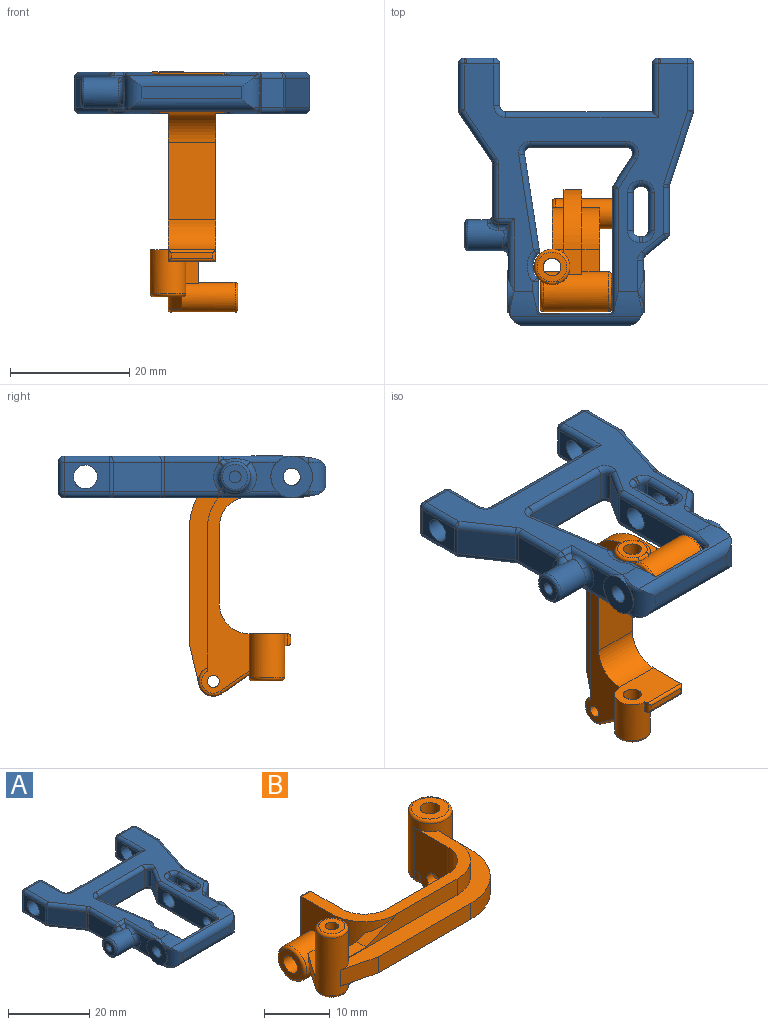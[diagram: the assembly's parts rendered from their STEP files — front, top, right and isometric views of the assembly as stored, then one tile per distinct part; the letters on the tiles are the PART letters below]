
ASSEMBLY  parts=2 mates=1
PART A: 193 faces, bbox 39.6x45x7 mm
  f0: cylinder r=1mm len=2.75mm, axis (0,1,0), area 1.5mm2, adj f15,f20,f177,f183
  f1: cylinder r=1mm len=2.75mm, axis (0,1,0), area 1.5mm2, adj f16,f26,f175,f186
  f2: cylinder r=1mm len=2.75mm, axis (0,-1,0), area 1.5mm2, adj f18,f23,f175,f183
  f3: plane 38.25x37.6mm, normal (0,0,1), area 421.9mm2, adj f7,f11,f21,f27,f57,f62,f65,f66
  f4: plane 38.25x37.6mm, normal (0,0,-1), area 421.9mm2, adj f8,f12,f24,f59,f63,f68,f69,f78
  f5: plane 16.75x2.05mm, normal (0,-1,0), area 34.3mm2, adj f14,f17,f184,f185
  f6: cylinder r=1mm len=2.75mm, axis (0,-1,0), area 1.5mm2, adj f13,f19,f177,f186
  f7: cylinder r=1mm len=20.85mm, axis (0,1,0), area 31.1mm2, adj f3,f54,f128,f186,f189
  f8: cylinder r=1mm len=20.85mm, axis (0,-1,0), area 31.1mm2, adj f4,f54,f131,f183,f187
  f9: cylinder r=1mm len=11.92mm, axis (1,0,0), area 7mm2, adj f36,f186,f189,f192
  f10: cylinder r=1mm len=11.92mm, axis (-1,0,0), area 7mm2, adj f36,f183,f187,f190
  f11: cylinder r=1mm len=5.15mm, axis (0,-1,0), area 6.4mm2, adj f3,f37,f139,f186,f192
  f12: cylinder r=1mm len=5.15mm, axis (0,1,0), area 6.4mm2, adj f4,f37,f140,f183,f190
  f13: torus R=2mm, axis (0,0,1), area 1.3mm2, adj f6,f14,f185,f186
  f14: cylinder r=3mm len=5mm, axis (0,0,-1), area 18.4mm2, adj f5,f13,f15,f19,f20,f177,f184,f185
  f15: torus R=2mm, axis (0,0,1), area 1.3mm2, adj f0,f14,f183,f184
  f16: torus R=2mm, axis (0,0,1), area 1.3mm2, adj f1,f17,f185,f186
  f17: cylinder r=3mm len=5mm, axis (0,0,-1), area 18.4mm2, adj f5,f16,f18,f23,f26,f175,f184,f185
  f18: torus R=2mm, axis (0,0,1), area 1.3mm2, adj f2,f17,f183,f184
  f19: plane 0.34x0.3mm, normal (1,0,0), area 0mm2, adj f6,f14,f177
  f20: plane 0.34x0.3mm, normal (1,0,0), area 0mm2, adj f0,f14,f177
  f21: cylinder r=1mm len=5.27mm, axis (0,-1,0), area 6.4mm2, adj f3,f45,f82,f177
  f22: plane 5x4.46mm, normal (-1,0,0), area 15.2mm2, adj f24,f27,f172,f175
  f23: plane 0.34x0.3mm, normal (-1,0,0), area 0mm2, adj f2,f17,f175
  f24: cylinder r=1mm len=12.25mm, axis (0,-1,0), area 14.5mm2, adj f4,f22,f95,f168,f170,f175
  f25: cylinder r=1mm len=0.18mm, axis (0,0,-1), area 0mm2, adj f44,f100,f164
  f26: plane 0.34x0.3mm, normal (-1,0,0), area 0mm2, adj f1,f17,f175
  f27: cylinder r=1mm len=12.25mm, axis (0,1,0), area 14.5mm2, adj f3,f22,f94,f171,f173,f175
  f28: cylinder r=1mm len=0.18mm, axis (0,0,-1), area 0mm2, adj f44,f99,f167
  f29: cylinder r=1mm len=5mm, axis (0,0,-1), area 7.9mm2, adj f30,f56,f145,f153
  f30: plane 5x0.53mm, normal (0,1,0), area 2.6mm2, adj f29,f31,f143,f151
  f31: cylinder r=1mm len=5mm, axis (0,0,-1), area 7.9mm2, adj f30,f32,f142,f150
  f32: plane 6.4x5mm, normal (1,0,0), area 19.4mm2, adj f31,f33,f144,f152,f182
  f33: cylinder r=1mm len=5mm, axis (0,0,-1), area 7.9mm2, adj f32,f34,f146,f154
  f34: plane 5x0.53mm, normal (0,-1,0), area 2.6mm2, adj f33,f35,f148,f156
  f35: cylinder r=1mm len=5mm, axis (0,0,-1), area 7.9mm2, adj f34,f56,f149,f157
  f36: plane 11.4x5mm, normal (0,1,0), area 57mm2, adj f9,f10,f188,f191
  f37: plane 5x4.8mm, normal (1,0,0), area 17.4mm2, adj f11,f12,f141,f180,f191
  f38: cylinder r=3mm len=5mm, axis (0,0,-1), area 21.7mm2, adj f133,f137,f138,f141
  f39: plane 15.99x5mm, normal (0.99,0.15,0), area 80.9mm2, adj f124,f132,f133,f134
  f40: plane 16.15x5mm, normal (0,-1,0), area 80.7mm2, adj f119,f123,f124,f125
  f41: plane 5x4.82mm, normal (-0.84,0.54,0), area 28.6mm2, adj f119,f122,f126,f127
  f42: plane 7.69x5mm, normal (-1,0,0), area 25.9mm2, adj f107,f112,f115,f118,f158
  f43: plane 8.13x5.51mm, normal (-0.83,-0.56,0), area 49.1mm2, adj f104,f113,f114,f118
  f44: plane 9.05x5mm, normal (-1,0,0), area 42.6mm2, adj f25,f28,f103,f104,f105,f165
  f45: plane 5x2.82mm, normal (1,0,0), area 10.5mm2, adj f21,f77,f86,f177
  f46: plane 5x3.57mm, normal (0.63,-0.78,0), area 23mm2, adj f67,f76,f77,f78
  f47: plane 7.76x5mm, normal (1,0,0), area 26.3mm2, adj f58,f66,f67,f68,f181
  f48: plane 12.3x5mm, normal (0.95,-0.31,0), area 64.7mm2, adj f57,f58,f59,f60
  f49: plane 7.84x5mm, normal (1,0,0), area 26.6mm2, adj f60,f65,f69,f70,f159
  f50: plane 5x5mm, normal (0,1,0), area 25mm2, adj f70,f75,f79,f80
  f51: plane 8x5mm, normal (-1,0,0), area 27.4mm2, adj f52,f80,f85,f87,f159
  f52: plane 24.6x5mm, normal (0,1,0), area 123mm2, adj f51,f88,f89,f90
  f53: plane 7x5mm, normal (1,0,0), area 22.4mm2, adj f90,f93,f96,f97,f158
  f54: plane 20.51x5mm, normal (-1,0,0), area 83.4mm2, adj f7,f8,f127,f179,f182,f188
  f55: plane 5x5mm, normal (0,1,0), area 25mm2, adj f97,f102,f106,f107
  f56: plane 6.4x5mm, normal (-1,0,0), area 19.4mm2, adj f29,f35,f147,f155,f181
  f57: cylinder r=1mm len=12.61mm, axis (-0.31,-0.95,0), area 20.3mm2, adj f3,f48,f61,f62
  f58: cylinder r=1mm len=5mm, axis (0,0,1), area 1.6mm2, adj f47,f48,f62,f63
  f59: cylinder r=1mm len=12.61mm, axis (0.31,0.95,0), area 20.3mm2, adj f4,f48,f63,f64
  f60: cylinder r=1mm len=5mm, axis (0,0,-1), area 1.6mm2, adj f48,f49,f61,f64
  f61: sphere r=1mm, area 0.3mm2, adj f57,f60,f65
  f62: torus R=2mm, axis (0,0,1), area 0.7mm2, adj f3,f57,f58,f66
  f63: torus R=2mm, axis (0,0,1), area 0.7mm2, adj f4,f58,f59,f68
  f64: sphere r=1mm, area 0.3mm2, adj f59,f60,f69
  f65: cylinder r=1mm len=7.84mm, axis (0,-1,0), area 12.3mm2, adj f3,f49,f61,f71
  f66: cylinder r=1mm len=7.76mm, axis (0,-1,0), area 12.2mm2, adj f3,f47,f62,f72
  f67: cylinder r=1mm len=5mm, axis (0,0,-1), area 4.4mm2, adj f46,f47,f72,f73
  f68: cylinder r=1mm len=7.76mm, axis (0,1,0), area 12.2mm2, adj f4,f47,f63,f73
  f69: cylinder r=1mm len=7.84mm, axis (0,1,0), area 12.3mm2, adj f4,f49,f64,f74
  f70: cylinder r=1mm len=5mm, axis (0,0,-1), area 7.9mm2, adj f49,f50,f71,f74
  f71: sphere r=1mm, area 1mm2, adj f65,f70,f75
  f72: sphere r=1mm, area 0.9mm2, adj f66,f67,f76
  f73: sphere r=1mm, area 0.9mm2, adj f67,f68,f78
  f74: sphere r=1mm, area 1mm2, adj f69,f70,f79
  f75: cylinder r=1mm len=5mm, axis (1,0,0), area 7.9mm2, adj f3,f50,f71,f81
  f76: cylinder r=1mm len=4.2mm, axis (-0.78,-0.63,0), area 7.2mm2, adj f3,f46,f72,f82
  f77: cylinder r=1mm len=5mm, axis (0,0,1), area 4.4mm2, adj f45,f46,f82,f83
  f78: cylinder r=1mm len=4.2mm, axis (0.78,0.63,0), area 7.2mm2, adj f4,f46,f73,f83
  f79: cylinder r=1mm len=5mm, axis (-1,0,0), area 7.9mm2, adj f4,f50,f74,f84
  f80: cylinder r=1mm len=5mm, axis (0,0,-1), area 7.9mm2, adj f50,f51,f81,f84
  f81: sphere r=1mm, area 2.1mm2, adj f75,f80,f85
  f82: torus R=2mm, axis (0,0,1), area 1.9mm2, adj f3,f21,f76,f77
  f83: torus R=2mm, axis (0,0,1), area 1.9mm2, adj f4,f77,f78,f86
  f84: sphere r=1mm, area 2.1mm2, adj f79,f80,f87
  f85: cylinder r=1mm len=9mm, axis (0,1,0), area 13.4mm2, adj f3,f51,f81,f88
  f86: cylinder r=1mm len=5.27mm, axis (0,1,0), area 6.4mm2, adj f4,f45,f83,f177
  f87: cylinder r=1mm len=9mm, axis (0,-1,0), area 13.4mm2, adj f4,f51,f84,f89
  f88: cylinder r=1mm len=25.6mm, axis (1,0,0), area 39.4mm2, adj f3,f52,f85,f91
  f89: cylinder r=1mm len=25.6mm, axis (-1,0,0), area 39.4mm2, adj f4,f52,f87,f92
  f90: cylinder r=1mm len=5mm, axis (0,0,1), area 7.9mm2, adj f52,f53,f91,f92
  f91: torus R=2mm, axis (0,0,1), area 3.4mm2, adj f3,f88,f90,f93
  f92: torus R=2mm, axis (0,0,1), area 3.4mm2, adj f4,f89,f90,f96
  f93: cylinder r=1mm len=7mm, axis (0,-1,0), area 11mm2, adj f3,f53,f91,f98
  f94: cylinder r=1mm len=2.55mm, axis (-1,0,0), area 2.3mm2, adj f3,f27,f99,f171
  f95: cylinder r=1mm len=2.55mm, axis (1,0,0), area 2.3mm2, adj f4,f24,f100,f168
  f96: cylinder r=1mm len=7mm, axis (0,1,0), area 11mm2, adj f4,f53,f92,f101
  f97: cylinder r=1mm len=5mm, axis (0,0,-1), area 7.9mm2, adj f53,f55,f98,f101
  f98: sphere r=1mm, area 1mm2, adj f93,f97,f102
  f99: sphere r=1mm, area 1mm2, adj f28,f94,f103,f169
  f100: sphere r=1mm, area 1mm2, adj f25,f95,f105,f166
  f101: sphere r=1mm, area 1mm2, adj f96,f97,f106
  f102: cylinder r=1mm len=5mm, axis (1,0,0), area 7.9mm2, adj f3,f55,f98,f108
  f103: cylinder r=1mm len=9.05mm, axis (0,1,0), area 14.2mm2, adj f3,f44,f99,f109
  f104: cylinder r=1mm len=5mm, axis (0,0,1), area 3mm2, adj f43,f44,f109,f110
  f105: cylinder r=1mm len=9.05mm, axis (0,-1,0), area 14.2mm2, adj f4,f44,f100,f110
  f106: cylinder r=1mm len=5mm, axis (-1,0,0), area 7.9mm2, adj f4,f55,f101,f111
  f107: cylinder r=1mm len=5mm, axis (0,0,-1), area 7.9mm2, adj f42,f55,f108,f111
  f108: sphere r=1mm, area 2.1mm2, adj f102,f107,f112
  f109: torus R=2mm, axis (0,0,1), area 1.3mm2, adj f3,f103,f104,f113
  f110: torus R=2mm, axis (0,0,1), area 1.3mm2, adj f4,f104,f105,f114
  f111: sphere r=1mm, area 2.1mm2, adj f106,f107,f115
  f112: cylinder r=1mm len=7.69mm, axis (0,1,0), area 12.1mm2, adj f3,f42,f108,f116
  f113: cylinder r=1mm len=8.69mm, axis (-0.56,0.83,0), area 15.4mm2, adj f3,f43,f109,f116
  f114: cylinder r=1mm len=8.69mm, axis (0.56,-0.83,0), area 15.4mm2, adj f4,f43,f110,f117
  f115: cylinder r=1mm len=7.69mm, axis (0,-1,0), area 12.1mm2, adj f4,f42,f111,f117
  f116: sphere r=1mm, area 0.6mm2, adj f112,f113,f118
  f117: sphere r=1mm, area 0.6mm2, adj f114,f115,f118
  f118: cylinder r=1mm len=5mm, axis (0,0,-1), area 3mm2, adj f42,f43,f116,f117
  f119: cylinder r=1mm len=5mm, axis (0,0,1), area 10.7mm2, adj f40,f41,f120,f121
  f120: torus R=2mm, axis (0,0,1), area 4.6mm2, adj f3,f119,f122,f123
  f121: torus R=2mm, axis (0,0,1), area 4.6mm2, adj f4,f119,f125,f126
  f122: cylinder r=1mm len=5.35mm, axis (0.54,0.84,0), area 9mm2, adj f3,f41,f120,f128
  f123: cylinder r=1mm len=16.15mm, axis (-1,0,0), area 25.4mm2, adj f3,f40,f120,f129
  f124: cylinder r=1mm len=5mm, axis (0,0,1), area 8.6mm2, adj f39,f40,f129,f130
  f125: cylinder r=1mm len=16.15mm, axis (1,0,0), area 25.4mm2, adj f4,f40,f121,f130
  f126: cylinder r=1mm len=5.35mm, axis (-0.54,-0.84,0), area 9mm2, adj f4,f41,f121,f131
  f127: cylinder r=1mm len=5mm, axis (0,0,-1), area 2.8mm2, adj f41,f54,f128,f131
  f128: sphere r=1mm, area 0.6mm2, adj f7,f122,f127
  f129: torus R=2mm, axis (0,0,1), area 3.7mm2, adj f3,f123,f124,f132
  f130: torus R=2mm, axis (0,0,1), area 3.7mm2, adj f4,f124,f125,f134
  f131: sphere r=1mm, area 0.6mm2, adj f8,f126,f127
  f132: cylinder r=1mm len=16.15mm, axis (0.15,-0.99,0), area 25.4mm2, adj f3,f39,f129,f135
  f133: cylinder r=1mm len=5mm, axis (0,0,-1), area 4.5mm2, adj f38,f39,f135,f136
  f134: cylinder r=1mm len=16.15mm, axis (-0.15,0.99,0), area 25.4mm2, adj f4,f39,f130,f136
  f135: sphere r=1mm, area 0.9mm2, adj f132,f133,f137
  f136: sphere r=1mm, area 0.8mm2, adj f133,f134,f138
  f137: torus R=4mm, axis (0,0,1), area 7.7mm2, adj f3,f38,f135,f139
  f138: torus R=4mm, axis (0,0,1), area 7.7mm2, adj f4,f38,f136,f140
  f139: sphere r=1mm, area 0.7mm2, adj f11,f137,f141
  f140: sphere r=1mm, area 0.4mm2, adj f12,f138,f141
  f141: cylinder r=1mm len=5mm, axis (0,0,-1), area 3.5mm2, adj f37,f38,f139,f140
  f142: torus R=2mm, axis (0,0,1), area 3.4mm2, adj f4,f31,f143,f144
  f143: cylinder r=1mm len=1mm, axis (-1,0,0), area 0.8mm2, adj f4,f30,f142,f145
  f144: cylinder r=1mm len=6.4mm, axis (0,1,0), area 10.1mm2, adj f4,f32,f142,f146
  f145: torus R=2mm, axis (0,0,1), area 3.4mm2, adj f4,f29,f143,f147
  f146: torus R=2mm, axis (0,0,1), area 3.4mm2, adj f4,f33,f144,f148
  f147: cylinder r=1mm len=6.4mm, axis (0,-1,0), area 10.1mm2, adj f4,f56,f145,f149
  f148: cylinder r=1mm len=1mm, axis (1,0,0), area 0.8mm2, adj f4,f34,f146,f149
  f149: torus R=2mm, axis (0,0,1), area 3.4mm2, adj f4,f35,f147,f148
  f150: torus R=2mm, axis (0,0,1), area 3.4mm2, adj f3,f31,f151,f152
  f151: cylinder r=1mm len=1mm, axis (1,0,0), area 0.8mm2, adj f3,f30,f150,f153
  f152: cylinder r=1mm len=6.4mm, axis (0,-1,0), area 10.1mm2, adj f3,f32,f150,f154
  f153: torus R=2mm, axis (0,0,1), area 3.4mm2, adj f3,f29,f151,f155
  f154: torus R=2mm, axis (0,0,1), area 3.4mm2, adj f3,f33,f152,f156
  f155: cylinder r=1mm len=6.4mm, axis (0,1,0), area 10.1mm2, adj f3,f56,f153,f157
  f156: cylinder r=1mm len=1mm, axis (-1,0,0), area 0.8mm2, adj f3,f34,f154,f157
  f157: torus R=2mm, axis (0,0,1), area 3.4mm2, adj f3,f35,f155,f156
  f158: cylinder r=2mm len=7mm, axis (-1,0,0), area 88mm2, adj f42,f53
  f159: cylinder r=2mm len=7mm, axis (-1,0,0), area 88mm2, adj f49,f51
  f160: cylinder r=2.6mm len=6.08mm, axis (1,0,0), area 79.2mm2, adj f164,f165,f166,f167,f168,f169,f170,f171
  f161: plane 4.2x4.2mm, normal (-1,0,0), area 10.7mm2, adj f163,f174
  f162: plane 2x2mm, normal (-1,0,0), area 3.1mm2, adj f163
  f163: cylinder r=1mm len=4.7mm, axis (1,0,0), area 29.5mm2, adj f161,f162
  f164: bspline ~1.16x1.09mm, area 0.3mm2, adj f25,f160,f165,f166
  f165: torus R=3.6mm, axis (-1,0,0), area 6.5mm2, adj f44,f160,f164,f167
  f166: bspline ~2.25x2.03mm, area 2.7mm2, adj f100,f160,f164,f168
  f167: bspline ~1.2x1.12mm, area 0.3mm2, adj f28,f160,f165,f169
  f168: cylinder r=1mm len=1.67mm, axis (1,0,0), area 1.7mm2, adj f24,f95,f160,f166,f170
  f169: bspline ~2.25x2.03mm, area 2.7mm2, adj f99,f160,f167,f171
  f170: bspline ~4.86x1.52mm, area 4mm2, adj f24,f160,f168,f172
  f171: cylinder r=1mm len=1.67mm, axis (-1,0,0), area 1.7mm2, adj f27,f94,f160,f169,f173
  f172: torus R=3.6mm, axis (-1,0,0), area 7.1mm2, adj f22,f160,f170,f173
  f173: bspline ~4.86x1.52mm, area 4mm2, adj f27,f160,f171,f172
  f174: torus R=2.1mm, axis (-1,0,0), area 11.9mm2, adj f160,f161
  f175: cylinder r=3.5mm len=7mm, axis (-1,0,0), area 7.6mm2, adj f1,f2,f17,f22,f23,f24,f26,f27
  f176: plane 7x7mm, normal (-1,0,0), area 31.9mm2, adj f175,f180
  f177: cylinder r=3.5mm len=7mm, axis (-1,0,0), area 6.6mm2, adj f0,f6,f14,f19,f20,f21,f45,f86
  f178: plane 7x7mm, normal (1,0,0), area 31.9mm2, adj f177,f179
  f179: cylinder r=1.45mm len=5.32mm, axis (-1,0,0), area 48.5mm2, adj f54,f178
  f180: cylinder r=1.45mm len=5.23mm, axis (-1,0,0), area 47.6mm2, adj f37,f176
  f181: cylinder r=2mm len=4mm, axis (1,0,0), area 44mm2, adj f47,f56
  f182: cylinder r=2mm len=4mm, axis (1,0,0), area 44mm2, adj f32,f54
  f183: cylinder r=17.03mm len=22.01mm, axis (1,0,0), area 40.4mm2, adj f0,f2,f4,f8,f10,f12,f15,f18
  f184: cylinder r=2mm len=21.69mm, axis (1,0,0), area 51.5mm2, adj f5,f14,f15,f17,f18,f183
  f185: cylinder r=2mm len=21.69mm, axis (1,0,0), area 51.5mm2, adj f5,f13,f14,f16,f17,f186
  f186: cylinder r=17.03mm len=22.01mm, axis (1,0,0), area 40.4mm2, adj f1,f3,f6,f7,f9,f11,f13,f16
  f187: bspline ~0.86x0.82mm, area 0.5mm2, adj f8,f10,f183,f188
  f188: cylinder r=0.5mm len=5mm, axis (0,0,1), area 3.9mm2, adj f36,f54,f187,f189
  f189: bspline ~0.86x0.82mm, area 0.5mm2, adj f7,f9,f186,f188
  f190: bspline ~0.86x0.82mm, area 0.5mm2, adj f10,f12,f183,f191
  f191: cylinder r=0.5mm len=5mm, axis (0,0,1), area 3.9mm2, adj f36,f37,f190,f192
  f192: bspline ~0.86x0.82mm, area 0.5mm2, adj f9,f11,f186,f191
PART B: 56 faces, bbox 40.9x21x15.2 mm
  f0: cylinder r=3mm len=6.4mm, axis (-1,0,0), area 63.4mm2, adj f1,f5,f6,f7,f11,f21,f25,f27
  f1: plane 1.15x0.2mm, normal (0,0,-1), area 0.1mm2, adj f0,f7,f11
  f2: plane 2x0.5mm, normal (0,0,-1), area 1mm2, adj f15,f17,f35,f54
  f3: cylinder r=7mm len=7mm, axis (0,0,-1), area 38.1mm2, adj f17,f20,f30,f32,f33
  f4: cylinder r=2.5mm len=10.75mm, axis (0,0,1), area 139.8mm2, adj f8,f18,f22,f26,f27,f29,f30,f33
  f5: plane 2x0.76mm, normal (1,0,0), area 0.5mm2, adj f0,f9,f27
  f6: cylinder r=3.35mm len=11mm, axis (0,0,-1), area 166.3mm2, adj f0,f7,f10,f11,f20,f25,f26,f46
  f7: cylinder r=3.35mm len=1.55mm, axis (0,0,-1), area 2.1mm2, adj f0,f1,f6,f46
  f8: plane 24.4x2.13mm, normal (0,-1,0), area 47.5mm2, adj f4,f9,f21,f27,f44
  f9: cylinder r=7mm len=7mm, axis (0,0,-1), area 22mm2, adj f5,f8,f21,f27
  f10: plane 4.08x3mm, normal (1,0,0), area 12.3mm2, adj f6,f19,f20,f26
  f11: plane 11x7.15mm, normal (-1,0,0), area 64.3mm2, adj f0,f1,f6,f12,f20,f38
  f12: cylinder r=5mm len=8mm, axis (0,0,-1), area 62.8mm2, adj f11,f13,f20,f21
  f13: plane 13x8mm, normal (0,1,0), area 104mm2, adj f12,f14,f20,f21
  f14: cylinder r=5mm len=8mm, axis (0,0,-1), area 62.8mm2, adj f13,f15,f20,f21
  f15: plane 11x6.5mm, normal (1,0,0), area 59.1mm2, adj f2,f14,f20,f35,f39,f55
  f16: plane 7x1mm, normal (0,1,0), area 7mm2, adj f52,f53,f54,f55
  f17: plane 8x6.5mm, normal (-1,0,0), area 37.2mm2, adj f2,f3,f20,f30,f35,f52
  f18: plane 23.71x3mm, normal (0,-1,0), area 49.9mm2, adj f4,f19,f20,f26,f32,f34
  f19: cylinder r=7mm len=7mm, axis (0,0,-1), area 33mm2, adj f10,f18,f20,f26
  f20: plane 27x14.15mm, normal (0,0,1), area 86.6mm2, adj f3,f6,f10,f11,f12,f13,f14,f15
  f21: plane 35x8mm, normal (0,0,-1), area 119.4mm2, adj f0,f8,f9,f12,f13,f14,f35,f41
  f22: plane 6.58x3mm, normal (-0.23,-0.97,0), area 20.3mm2, adj f4,f23,f26,f27
  f23: plane 20x3mm, normal (0,-1,0), area 60mm2, adj f22,f24,f26,f27
  f24: cylinder r=10mm len=10mm, axis (0,0,-1), area 47.1mm2, adj f23,f25,f26,f27
  f25: plane 4.23x3mm, normal (1,0,0), area 10mm2, adj f0,f6,f24,f26,f27
  f26: plane 36.58x14.23mm, normal (0,0,1), area 123.1mm2, adj f4,f6,f10,f18,f19,f22,f23,f24
  f27: plane 36.58x10.76mm, normal (0,0,-1), area 113.6mm2, adj f0,f4,f5,f8,f9,f22,f23,f24
  f28: plane 4x4mm, normal (0,0,1), area 9.4mm2, adj f41,f51
  f29: plane 5.73x4.05mm, normal (-0.82,0.57,0), area 10.3mm2, adj f4,f30,f35,f45
  f30: plane 10.15x5.96mm, normal (0,0,1), area 35.7mm2, adj f3,f4,f17,f29,f33,f35
  f31: plane 5.7x5.7mm, normal (0,0,1), area 18.4mm2, adj f40,f50
  f32: plane 6.79x3.05mm, normal (-0.4,0,0.92), area 7.1mm2, adj f3,f18,f33,f34
  f33: plane 5.81x3.67mm, normal (0,1,0), area 17.7mm2, adj f3,f4,f30,f32,f34
  f34: plane 4.1x2mm, normal (0.01,0,1), area 7.9mm2, adj f4,f18,f32,f33
  f35: cylinder r=3mm len=7.4mm, axis (-1,0,0), area 109.5mm2, adj f2,f15,f17,f21,f29,f30,f45,f49
  f36: plane 5x5mm, normal (-1,0,0), area 12.6mm2, adj f39,f49
  f37: plane 5.01x5mm, normal (1,0,0), area 12.6mm2, adj f38,f47,f48
  f38: cylinder r=1.5mm len=6.9mm, axis (1,0,0), area 55.3mm2, adj f11,f37,f42
  f39: cylinder r=1.5mm len=7.9mm, axis (1,0,0), area 74.5mm2, adj f15,f36
  f40: cylinder r=1.5mm len=12mm, axis (0,0,1), area 113.1mm2, adj f31,f43
  f41: cylinder r=1mm len=11.75mm, axis (0,0,1), area 73.8mm2, adj f21,f28
  f42: cylinder r=3.35mm len=4.1mm, axis (0,0,1), area 9.1mm2, adj f38
  f43: plane 5.7x4.76mm, normal (0,0,-1), area 15.7mm2, adj f0,f40,f46
  f44: torus R=2mm, axis (0,0,1), area 6mm2, adj f4,f8,f21,f45
  f45: cylinder r=0.5mm len=5.14mm, axis (-0.57,-0.82,0), area 4.5mm2, adj f21,f29,f35,f44
  f46: torus R=2.85mm, axis (0,0,1), area 10.8mm2, adj f0,f6,f7,f43
  f47: torus R=2.5mm, axis (-1,0,0), area 12.1mm2, adj f0,f37,f48
  f48: bspline ~2.82x0.81mm, area 1.6mm2, adj f6,f37,f47
  f49: torus R=2.5mm, axis (-1,0,0), area 13.9mm2, adj f35,f36
  f50: torus R=2.85mm, axis (0,0,1), area 15.6mm2, adj f6,f31
  f51: torus R=2mm, axis (0,0,1), area 11.4mm2, adj f4,f28
  f52: cylinder r=0.5mm len=8mm, axis (0,0,1), area 5.9mm2, adj f16,f17,f53,f54
  f53: cylinder r=0.5mm len=2mm, axis (1,0,0), area 1.2mm2, adj f16,f20,f52,f55
  f54: cylinder r=0.5mm len=2mm, axis (-1,0,0), area 1.2mm2, adj f2,f16,f52,f55
  f55: cylinder r=0.5mm len=8mm, axis (0,0,-1), area 5.9mm2, adj f15,f16,f53,f54
PLACE A t=(0.72,7.22,4.36)mm
PLACE B rot(axis=(0.71,0,0.71),180deg) t=(3.76,-46.64,-5.05)mm
MATE revolute A.f175 <-> B.f6  axis (-1,0,0) through (9.91,-52.91,7.86)mm
